# Revit family: R-MTD-282
name_source: partatom
category: Portes
units: mm (PartAtom-declared; Revit-internal decimal feet)

## family parameters
Couper avec des vides une fois chargée = Non
Hôte = Mur
Partagée = Non
Point de calcul de pièce = Non
Toujours verticalement = Oui

## types (3) — shared parameters
1 Vantail = Oui
2 Vantaux = Non
Angle Rail 1 = 1.00°
Angle Rail 2 = 1.00°
Butée en L = Non
Butée en U = Oui
Construction analytique = <Aucun>
DAS = Non
DC Fixation_Rail = 150 mm  [stored 0.492126 ft]
Ep Butée = 178 mm  [stored 0.58399 ft]
Ep Chicane Murale = 200 mm  [stored 0.656168 ft]
Ep Face Coté Baie = 10 mm  [stored 0.0328084 ft]
Ep Face Coté Opposé Baie = 10 mm  [stored 0.0328084 ft]
Ep Fond Butée = 11 mm  [stored 0.0360892 ft]
Ep Rail = 3 mm  [stored 0.00984252 ft]
Ep Vantail = 82 mm  [stored 0.269029 ft]
Fabricant = MALERBA
Fixation Linteau = Oui
Fixation sous Dalle = Non
Grille Vantail Principal = Oui
Grille Vantail Secondaire = Non
Grille toute hauteur = Non
Hauteur Baie = 2500 mm  [stored 8.2021 ft]
Hauteur Profil Rail = 44 mm  [stored 0.144357 ft]
Hauteur chandelle support grille = 180 mm  [stored 0.590551 ft]
Hauteur sous Dalle = 3000 mm  [stored 9.84252 ft]
Ht Fixation Linteau = 430 mm
Ht Portillon = 2000 mm  [stored 6.56168 ft]
Jeu Portillon Bas = 51 mm
Jeu Portillon Coté Opposé Pivot = 10 mm  [stored 0.0328084 ft]
Jeu Portillon Coté Pivot = 10 mm  [stored 0.0328084 ft]
Jeu Portillon Haut = 10 mm  [stored 0.0328084 ft]
Jeu Vantail Bas = 10 mm  [stored 0.0328084 ft]
Larg Portillon = 900 mm  [stored 2.95276 ft]
Larg Vantail Primaire Asymétrique = 2400 mm
Largeur Baie = 2500 mm  [stored 8.2021 ft]
Lgt Fix Vantail Primaire = 5325 mm  [stored 17.4705 ft]
Lgt Fix Vantail Second = 5325 mm  [stored 17.4705 ft]
Lgt Rail Second = 5825 mm  [stored 19.1109 ft]
Mat Ame = Prépeint
Mat Grille = Grille
Mat Quinc = Acier galvanisé
Mat Support = Peinture Laquée PMT - Gris Anthracite - RAL 7016
Materiaux_Dominant = Métal
Montage sur Mur Perpendiculaire = Non
Position Vantail Mur = 91 mm  [stored 0.298556 ft]
Prof Butée = 260 mm  [stored 0.853018 ft]
Prof Chicane Murale = 50 mm  [stored 0.164042 ft]
Prof Coté Butée = 71 mm
Profondeur Rail = 49 mm  [stored 0.160761 ft]
Rec Arrière = 215 mm
Rec Avant = 160 mm  [stored 0.524934 ft]
Rec Haut = 200 mm  [stored 0.656168 ft]
Retours Rails = 17 mm
URL = https://www.malerba.fr
Vantaux Asymétriques = Non
lgt Rail Primaire = 5825 mm  [stored 19.1109 ft]
zero-valued in all types: DC Jeu Avant, DC Jeu Haut, DC Portillon, DC Profil Butée, Désax 2V Asymétrique, Thermique (W/m2.°K)

## type names (no varying parameters)
- MTD-282 2500x3500
- MTD-282 4000x3500
- MTD-282 5000x3500

note: [stored X ft] marks values corroborated as IEEE doubles in the binary element streams (Revit-internal decimal feet)

## geometry (parser evidence)
native form markers: Blend x12
no freeform markers — native parametric forms only
